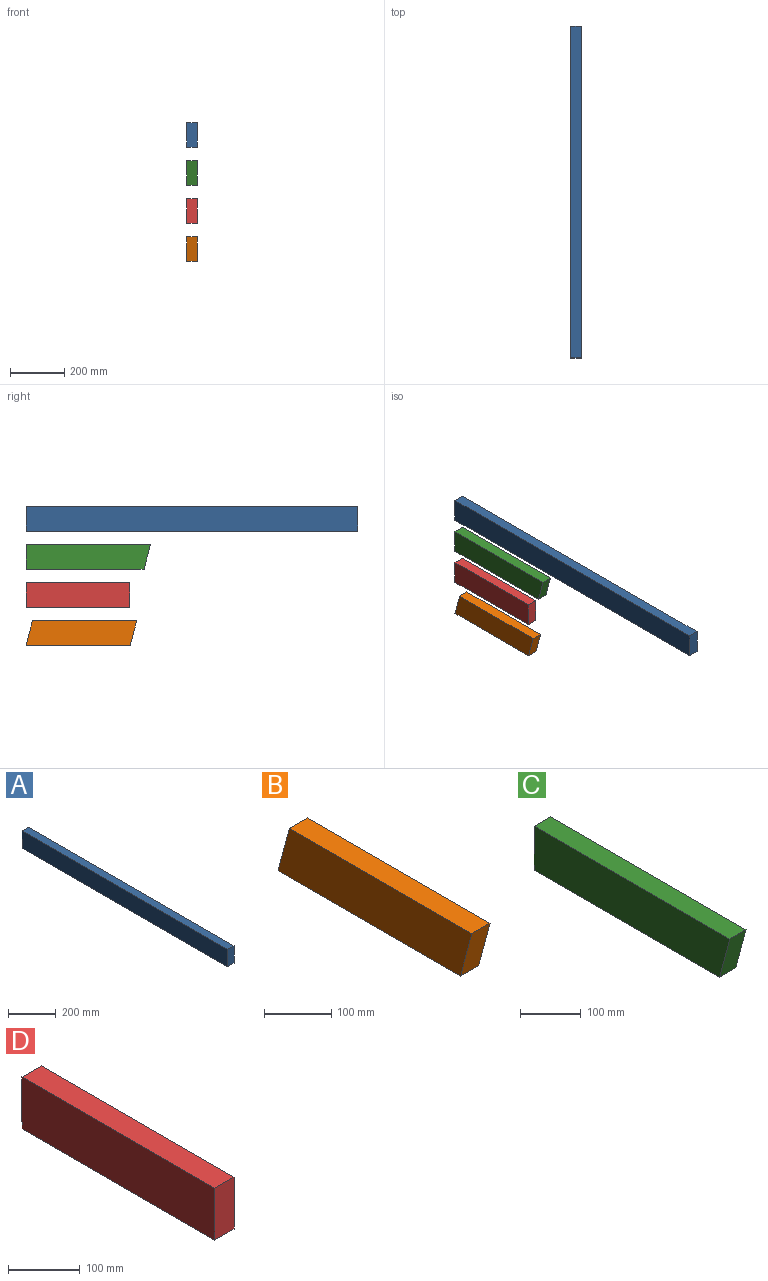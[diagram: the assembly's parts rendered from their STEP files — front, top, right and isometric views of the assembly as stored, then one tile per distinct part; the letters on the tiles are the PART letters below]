
ASSEMBLY  parts=4 mates=3
PART A: 6 faces, bbox 38.1x1219.2x88.9 mm
  f0: plane 1219.2x88.9mm, normal (-1,0,0), area 108386.9mm2, adj f1,f3,f4,f5
  f1: plane 1219.2x38.1mm, normal (0,0,-1), area 46451.5mm2, adj f0,f2,f4,f5
  f2: plane 1219.2x88.9mm, normal (1,0,0), area 108386.9mm2, adj f1,f3,f4,f5
  f3: plane 1219.2x38.1mm, normal (0,0,1), area 46451.5mm2, adj f0,f2,f4,f5
  f4: plane 88.9x38.1mm, normal (0,-1,0), area 3387.1mm2, adj f0,f1,f2,f3
  f5: plane 88.9x38.1mm, normal (0,1,0), area 3387.1mm2, adj f0,f1,f2,f3
PART B: 6 faces, bbox 38.1x406.4x88.9 mm
  f0: plane 382.58x38.1mm, normal (0,0,1), area 14576.3mm2, adj f1,f3,f4,f5
  f1: plane 406.4x88.9mm, normal (-1,0,0), area 34011.3mm2, adj f0,f2,f4,f5
  f2: plane 382.58x38.1mm, normal (0,0,-1), area 14576.3mm2, adj f1,f3,f4,f5
  f3: plane 406.4x88.9mm, normal (1,0,0), area 34011.3mm2, adj f0,f2,f4,f5
  f4: plane 88.9x38.1mm, normal (0,0.97,0.26), area 3506.6mm2, adj f0,f1,f2,f3
  f5: plane 88.9x38.1mm, normal (0,-0.97,-0.26), area 3506.6mm2, adj f0,f1,f2,f3
PART C: 6 faces, bbox 38.1x457.2x88.9 mm
  f0: plane 457.2x88.9mm, normal (-1,0,0), area 39586.3mm2, adj f1,f3,f4,f5
  f1: plane 433.38x38.1mm, normal (0,0,-1), area 16511.8mm2, adj f0,f2,f4,f5
  f2: plane 457.2x88.9mm, normal (1,0,0), area 39586.3mm2, adj f1,f3,f4,f5
  f3: plane 457.2x38.1mm, normal (0,0,1), area 17419.3mm2, adj f0,f2,f4,f5
  f4: plane 88.9x38.1mm, normal (0,1,0), area 3387.1mm2, adj f0,f1,f2,f3
  f5: plane 88.9x38.1mm, normal (0,-0.97,-0.26), area 3506.6mm2, adj f0,f1,f2,f3
PART D: 6 faces, bbox 38.1x381x88.9 mm
  f0: plane 381x88.9mm, normal (-1,0,0), area 33870.9mm2, adj f1,f3,f4,f5
  f1: plane 381x38.1mm, normal (0,0,-1), area 14516.1mm2, adj f0,f2,f4,f5
  f2: plane 381x88.9mm, normal (1,0,0), area 33870.9mm2, adj f1,f3,f4,f5
  f3: plane 381x38.1mm, normal (0,0,1), area 14516.1mm2, adj f0,f2,f4,f5
  f4: plane 88.9x38.1mm, normal (0,-1,0), area 3387.1mm2, adj f0,f1,f2,f3
  f5: plane 88.9x38.1mm, normal (0,1,0), area 3387.1mm2, adj f0,f1,f2,f3
PLACE A at identity fixed
PLACE B t=(0,0,-419.1)mm
PLACE C t=(0,0,-139.7)mm
PLACE D t=(0,0,-279.4)mm
MATE fastened C.f2 <-> A.f2  axis (1,0,0) through (38.1,0,-50.8)mm
MATE fastened B.f3 <-> D.f2  axis (1,0,0) through (38.1,0,-419.1)mm
MATE fastened D.f2 <-> C.f2  axis (1,0,0) through (38.1,0,-190.5)mm
